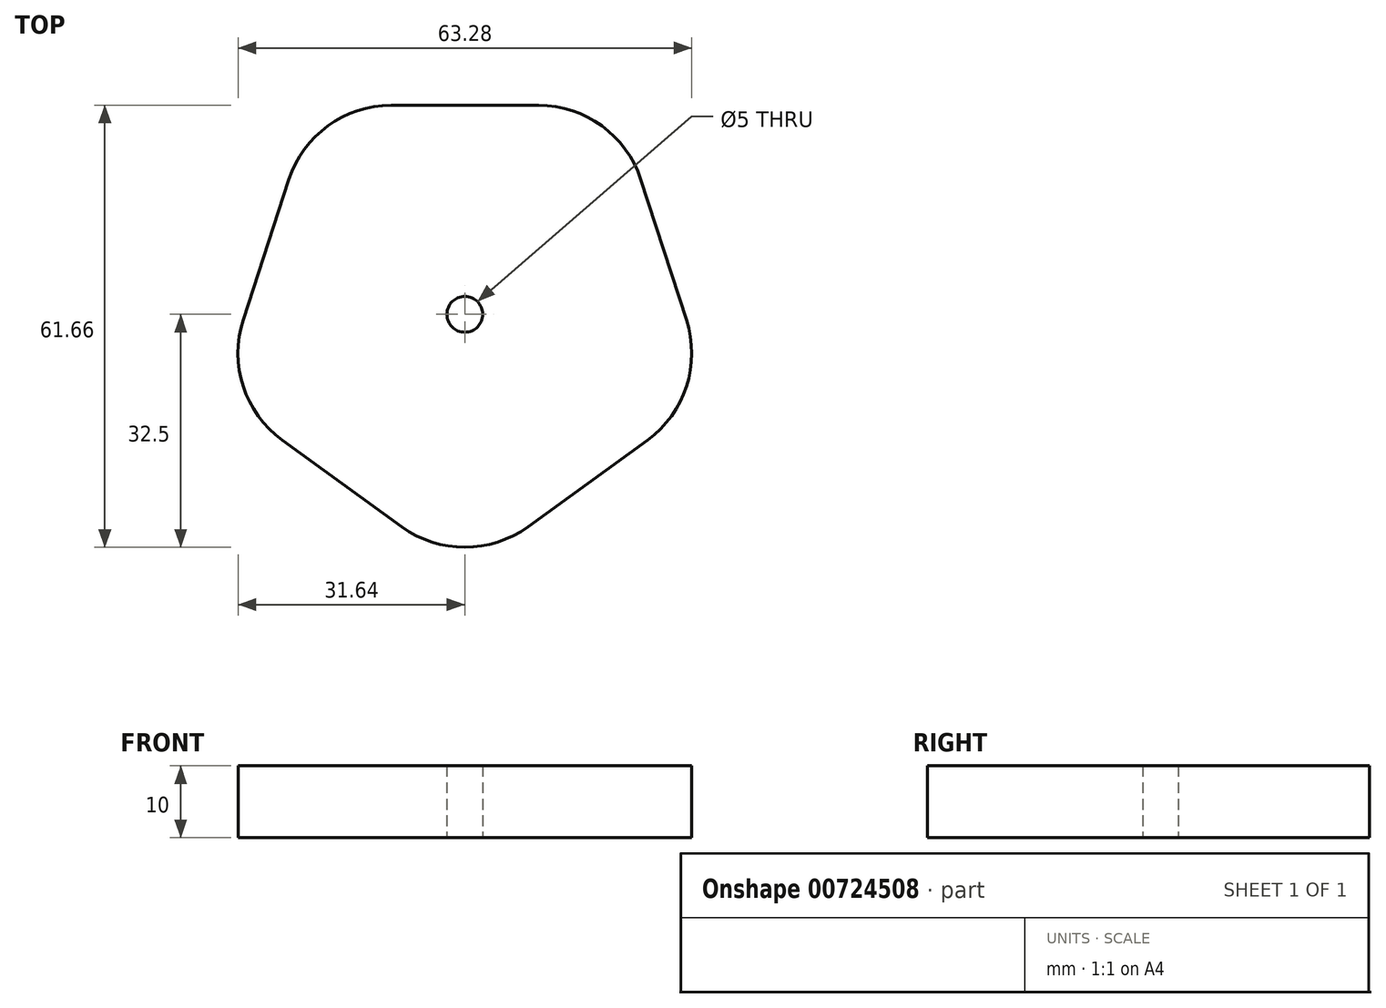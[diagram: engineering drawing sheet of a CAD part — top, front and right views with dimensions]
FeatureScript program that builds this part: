
annotation { "Feature Type Name" : "Feature", "Feature Type Description" : "" }
export const myFeature = defineFeature(function(context is Context, id is Id, definition is map)
    precondition{}
    {
        {
            var Q0;
            Q0=qCreatedBy(makeId("Top.planeOp"),FACE);
            var sketch = newSketch(context, id + "F0", { "sketchPlane" : qUnion([Q0])});
            skCircle(sketch, "E0.cCircle", {"center": v(0, 0) * mm, "radius": 29.16 * mm, "construction": true});
            skLineSegment(sketch, "E0.0", {"start": v(-10.29, 29.16) * mm, "end": v(10.29, 29.16) * mm});
            skLineSegment(sketch, "E0.1", {"start": v(24.55, 18.8) * mm, "end": v(30.9, -0.77) * mm});
            skLineSegment(sketch, "E0.2", {"start": v(25.46, -17.54) * mm, "end": v(8.82, -29.64) * mm});
            skLineSegment(sketch, "E0.3", {"start": v(-8.82, -29.64) * mm, "end": v(-25.46, -17.54) * mm});
            skLineSegment(sketch, "E0.4", {"start": v(-30.9, -0.77) * mm, "end": v(-24.55, 18.8) * mm});
            skPoint(sketch, "E0.0.midPoint", {"position": v(0, 29.16) * mm});
            skPoint(sketch, "E1.visualSharp", {"position": v(-21.18, 29.16) * mm});
            skArc(sketch, "E1.filletArc", {"start": v(-10.29, 29.16) * mm, "mid": v(-19.1, 26.3) * mm, "end": v(-24.55, 18.8) * mm});
            skPoint(sketch, "E2.visualSharp", {"position": v(-34.28, -11.14) * mm});
            skArc(sketch, "E2.filletArc", {"start": v(-30.9, -0.77) * mm, "mid": v(-30.9, -10.04) * mm, "end": v(-25.46, -17.54) * mm});
            skPoint(sketch, "E3.visualSharp", {"position": v(0, -36.04) * mm});
            skArc(sketch, "E3.filletArc", {"start": v(-8.82, -29.64) * mm, "mid": v(0, -32.5) * mm, "end": v(8.82, -29.64) * mm});
            skPoint(sketch, "E4.visualSharp", {"position": v(34.28, -11.14) * mm});
            skArc(sketch, "E4.filletArc", {"start": v(25.46, -17.54) * mm, "mid": v(30.9, -10.04) * mm, "end": v(30.9, -0.77) * mm});
            skPoint(sketch, "E5.visualSharp", {"position": v(21.18, 29.16) * mm});
            skArc(sketch, "E5.filletArc", {"start": v(24.55, 18.8) * mm, "mid": v(19.1, 26.3) * mm, "end": v(10.29, 29.16) * mm});
            skCircle(sketch, "E6", {"center": v(0, 0) * mm, "radius": 2.5 * mm});
            skSolve(sketch);
        }
        {
            var Q0;
            Q0=qSketchRegion(id+"F0",true);
            extrude(context, id + "F1", {"entities" : qUnion([Q0]), "depth" : 10 * mm, "offsetDistance" : 25 * mm});
        }
    });
